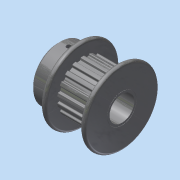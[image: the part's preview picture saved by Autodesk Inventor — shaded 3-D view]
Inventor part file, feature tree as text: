
AUTODESK INVENTOR PART (.ipt)
format: ipt  version: 2015 (Build 190159000, 159)  size: 440,832 bytes
history: native  units: in
note: dims shown in document units (in); Inventor stores cm internally (conversion verified against a paired STEP export)
features: imported_body x3, other x1, extrude x1, sketch x1
ambient origin geometry x8: Origin, YZ Plane, XZ Plane, XY Plane, X Axis, Y Axis, Z Axis, Center Point
bodies: Solid1 (feature_tree), Solid2 (feature_tree), Solid3 (feature_tree)
feature tree (6):
  other  "A_6Z23M018DF09061"
  extrude  "Extrusion1"  Depth=0.3937in TaperAngle=0.0deg
  imported_body  "Base1"
  imported_body  "Base2"
  imported_body  "Base3"
  sketch  "Sketch1"  dims[d0=0.315in d1=0.3937in d2=0.0in]
